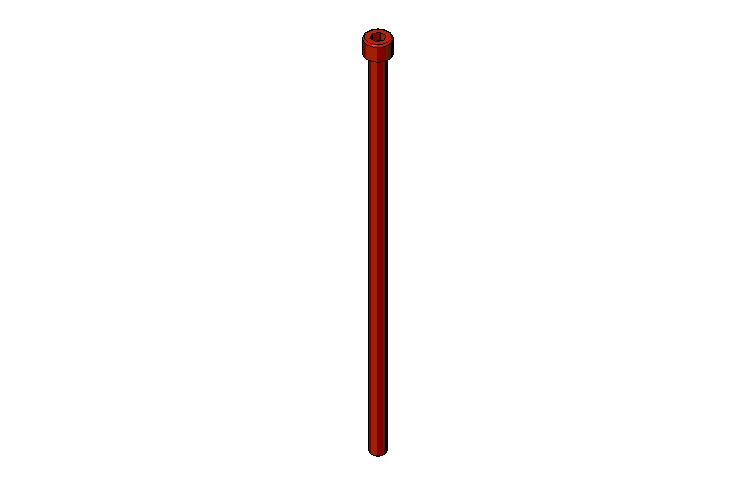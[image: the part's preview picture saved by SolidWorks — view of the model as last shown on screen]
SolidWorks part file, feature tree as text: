
SOLIDWORKS PART (.sldprt)
format: sldprt  version: not decoded by parser v0  size: 206,336 bytes
history: native  units: mm
features: plane x3, sketch x3, material x1, extrude x1, chamfer x1, revolve x1, cut_extrude x1 (+10 scaffold rows collapsed)
feature tree (21):
  scaffold x10  (default folders/planes/origin — collapsed)
  material  "Matériau <non spécifié>"
  plane  "Plan1"
  plane  "Plan2"
  plane  "Plan3"
  sketch  "Esquisse2"  dims[Diamètre nominal=5.0mm]
  extrude  "Base-Extrusion"  Depth=135mm Longueur sous tête=135mm
  chamfer  "Chanfrein1"  Distance=0.5mm Angle=45deg
  sketch  "Esquisse5"  dims[c1.D2=0.55mm c1.Hauteur tête=2.0mm c1.Cote sur plats=5.5mm c1.D3=~2.780036mm c2.D3=30.0deg c2.D4=2.75mm c2.Diamètre tête=8.5mm c2.Diamètre nominal=3.0mm c2.D1=4.25mm c3.D3=3.0mm c4.D3=60.0deg c4.Diamètre nominal=5.5mm c4.Cote sur plats=4.0mm c4.D4=2.75mm c4.D5=2.0mm]
  revolve  "Boss.-Révol.1"  Angle=360deg
  sketch  "Esquisse7"  dims[c1.D1=~2.410714mm c2.D1=30.0deg c2.D2=~1.370242mm c3.D2=30.0deg c3.D3=2.5mm]
  cut_extrude  "Enlèv. mat.-Extru.1"  Depth=2.75mm
decode coverage: 7 of 7 modeling features carry decoded parameters
note: ~ marks probable driven/reference dimensions
note: suppression state not decoded; provenance and decode notes live in map.json
